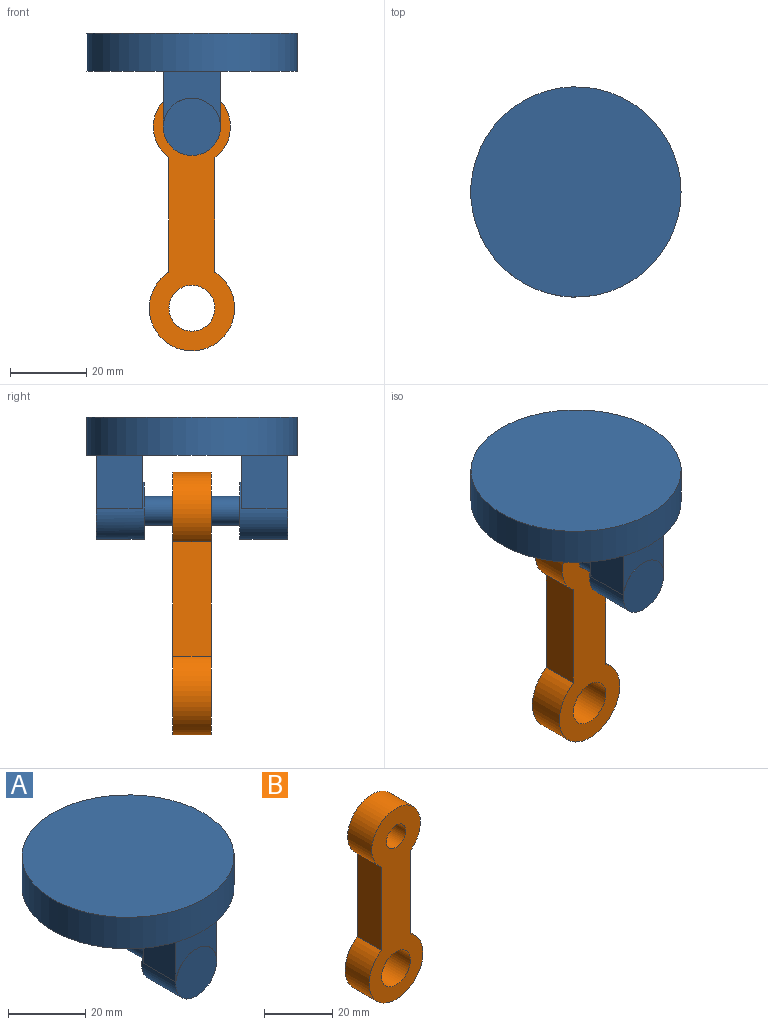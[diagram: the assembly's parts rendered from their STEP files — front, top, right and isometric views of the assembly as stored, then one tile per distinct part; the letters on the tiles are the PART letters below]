
ASSEMBLY  parts=2 mates=1
PART A: 20 faces, bbox 55x55x32 mm
  f0: plane 13.79x12mm, normal (-1,0,0), area 165.4mm2, adj f1,f3,f8,f19
  f1: plane 15x14.5mm, normal (0,-1,0), area 129.2mm2, adj f0,f2,f8,f15,f19
  f2: plane 14.5x12mm, normal (1,0,0), area 174mm2, adj f1,f3,f15,f19
  f3: plane 15x14.5mm, normal (0,1,0), area 129.2mm2, adj f0,f2,f8,f15,f19
  f4: plane 14.5x12mm, normal (-1,0,0), area 165.5mm2, adj f5,f7,f13,f14,f16,f19
  f5: plane 15x14.5mm, normal (0,-1,0), area 129.2mm2, adj f4,f6,f14,f16,f19
  f6: plane 14.5x12mm, normal (1,0,0), area 174mm2, adj f5,f7,f16,f19
  f7: plane 15x14.5mm, normal (0,1,0), area 217.5mm2, adj f4,f6,f16,f19
  f8: cylinder r=7.5mm len=15mm, axis (0,1,0), area 314.9mm2, adj f0,f1,f3,f9,f11,f15
  f9: plane 15x15mm, normal (0,-1,0), area 176.7mm2, adj f8
  f10: cylinder r=3.75mm len=25mm, axis (0,1,0), area 589mm2, adj f11,f12
  f11: plane 15x15mm, normal (0,1,0), area 132.5mm2, adj f8,f10
  f12: plane 15x15mm, normal (0,-1,0), area 132.5mm2, adj f10,f14
  f13: plane 15x8.21mm, normal (0,1,0), area 88.4mm2, adj f4,f14,f16
  f14: cylinder r=7.5mm len=15mm, axis (0,1,0), area 315.1mm2, adj f4,f5,f12,f13,f16
  f15: plane 12x0.03mm, normal (0,0,-1), area 0.4mm2, adj f1,f2,f3,f8
  f16: plane 15x12mm, normal (0,0,-1), area 0.6mm2, adj f4,f5,f6,f7,f13,f14
  f17: cylinder r=27.5mm len=55mm, axis (0,0,-1), area 1727.9mm2, adj f18,f19
  f18: plane 55x55mm, normal (0,0,1), area 2375.8mm2, adj f17
  f19: plane 55x55mm, normal (0,0,-1), area 2015.8mm2, adj f0,f1,f2,f3,f4,f5,f6,f7
PART B: 8 faces, bbox 22.3x10x68.7 mm
  f0: plane 29.93x10mm, normal (1,0,0), area 299.3mm2, adj f1,f5,f6,f7
  f1: cylinder r=10.08mm len=20.16mm, axis (0,1,0), area 504.9mm2, adj f0,f2,f6,f7
  f2: plane 29.93x10mm, normal (-1,0,0), area 299.3mm2, adj f1,f5,f6,f7
  f3: cylinder r=4mm len=10mm, axis (0,1,0), area 251.3mm2, adj f6,f7
  f4: cylinder r=6mm len=12mm, axis (0,1,0), area 377mm2, adj f6,f7
  f5: cylinder r=11.16mm len=22.33mm, axis (0,1,0), area 574.8mm2, adj f0,f2,f6,f7
  f6: plane 68.7x22.33mm, normal (0,-1,0), area 876.3mm2, adj f0,f1,f2,f3,f4,f5
  f7: plane 68.7x22.33mm, normal (0,1,0), area 876.3mm2, adj f0,f1,f2,f3,f4,f5
PLACE A t=(-5.5,15.34,38.84)mm
PLACE B t=(-5.5,20.34,38.84)mm
MATE cylindrical B.f3 <-> A.f10  axis (0,1,0) through (-5.5,15.34,38.84)mm
